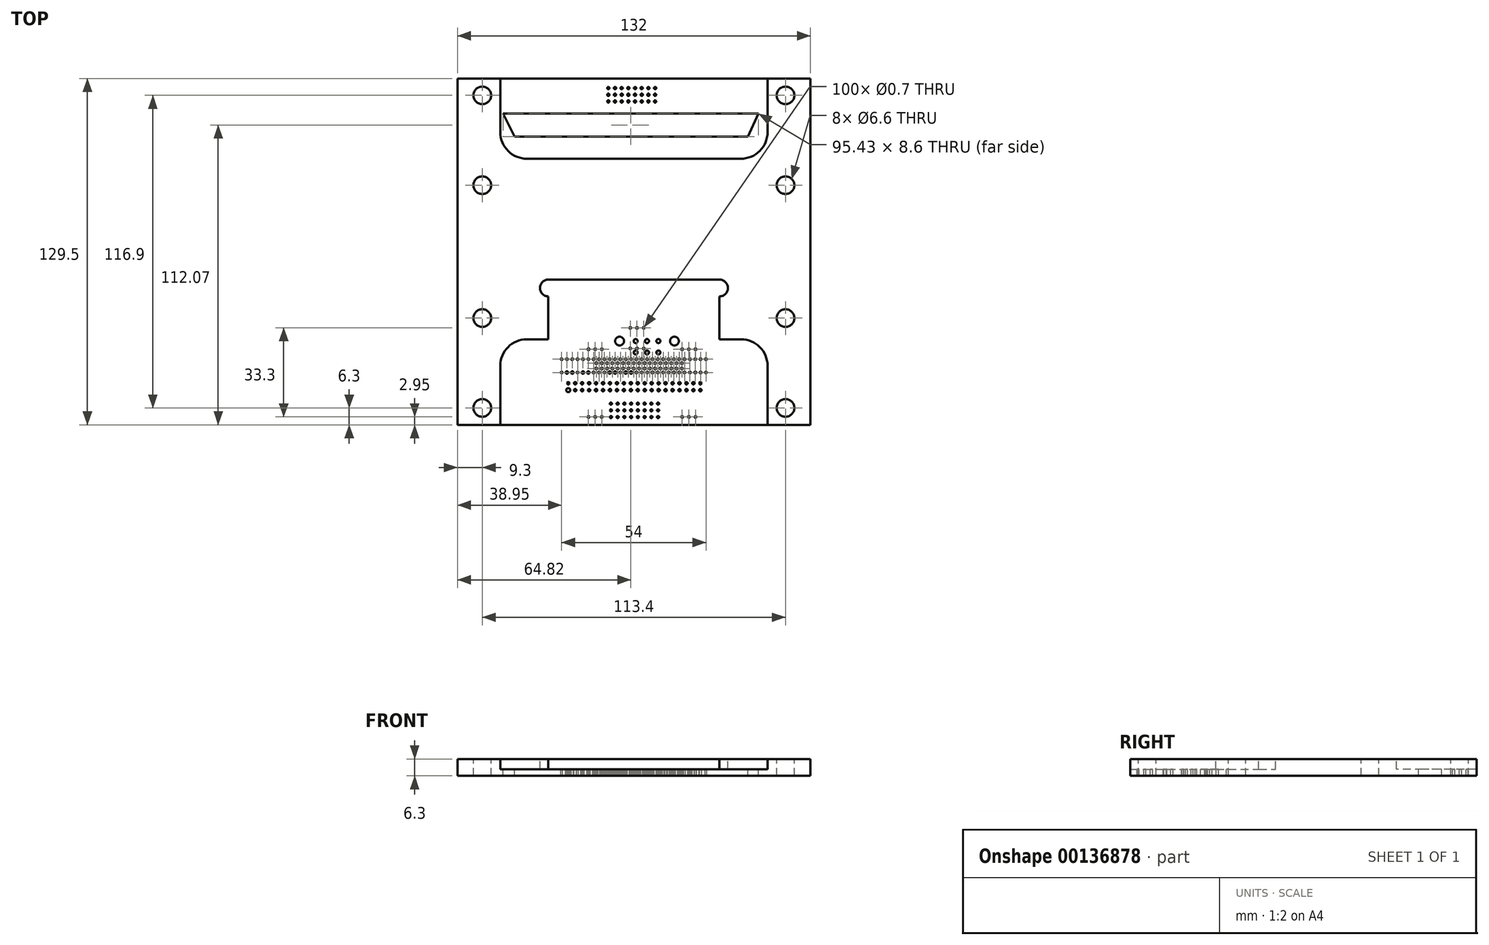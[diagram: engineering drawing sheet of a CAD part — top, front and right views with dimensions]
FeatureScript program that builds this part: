
annotation { "Feature Type Name" : "Feature", "Feature Type Description" : "" }
export const myFeature = defineFeature(function(context is Context, id is Id, definition is map)
    precondition{}
    {
        {
            var Q0;
            Q0=qCreatedBy(makeId("Top.planeOp"),FACE);
            var sketch = newSketch(context, id + "F0", { "sketchPlane" : qUnion([Q0])});
            skLineSegment(sketch, "E0.bottom", {"start": v(-66, 64.75) * mm, "end": v(66, 64.75) * mm});
            skLineSegment(sketch, "E0.top", {"start": v(-66, -64.75) * mm, "end": v(66, -64.75) * mm});
            skLineSegment(sketch, "E0.left", {"start": v(-66, 64.75) * mm, "end": v(-66, -64.75) * mm});
            skLineSegment(sketch, "E0.right", {"start": v(66, 64.75) * mm, "end": v(66, -64.75) * mm});
            skPoint(sketch, "E0.middle", {"position": v(0, 0) * mm});
            skSolve(sketch);
        }
        {
            var Q0;
            Q0 = qSketchRegion(id + "F0", true);
            extrude(context, id + "F1", {"entities" : qUnion([Q0]), "depth" : 6.3 * mm});
        }
        {
            var Q0;
            Q0=makeQuery(id+"F1.opExtrude","CAP_FACE",FACE,{"disambiguationData":[OSD([sQuery(id+"F0.wireOp",EDGE,"E0.bottom"),sQuery(id+"F0.wireOp",EDGE,"E0.top"),sQuery(id+"F0.wireOp",EDGE,"E0.left"),sQuery(id+"F0.wireOp",EDGE,"E0.right")])],"isStart":false});
            var sketch = newSketch(context, id + "F2", { "sketchPlane" : qUnion([Q0])});
            skLineSegment(sketch, "E1.bottom", {"start": v(-50, -64.75) * mm, "end": v(50, -64.75) * mm});
            skLineSegment(sketch, "E1.top", {"start": v(-40, -32.75) * mm, "end": v(-32, -32.75) * mm});
            skLineSegment(sketch, "E1.left", {"start": v(-50, -64.75) * mm, "end": v(-50, -42.75) * mm});
            skLineSegment(sketch, "E1.right", {"start": v(50, -64.75) * mm, "end": v(50, -42.75) * mm});
            skPoint(sketch, "E2.visualSharp", {"position": v(-50, -32.75) * mm});
            skArc(sketch, "E2.filletArc", {"start": v(-40, -32.75) * mm, "mid": v(-47.07, -35.68) * mm, "end": v(-50, -42.75) * mm});
            skPoint(sketch, "E3.visualSharp", {"position": v(50, -32.75) * mm});
            skArc(sketch, "E3.filletArc", {"start": v(50, -42.75) * mm, "mid": v(47.07, -35.68) * mm, "end": v(40, -32.75) * mm});
            skLineSegment(sketch, "E4.left", {"start": v(-32, -32.75) * mm, "end": v(-32, -16.75) * mm});
            skLineSegment(sketch, "E4.right", {"start": v(32, -32.75) * mm, "end": v(32, -16.75) * mm});
            skLineSegment(sketch, "E5.trimOffspring", {"start": v(32, -32.75) * mm, "end": v(40, -32.75) * mm});
            skLineSegment(sketch, "E6", {"start": v(-32, -10.45) * mm, "end": v(32, -10.45) * mm});
            skArc(sketch, "E7", {"start": v(32, -16.75) * mm, "mid": v(35.15, -13.6) * mm, "end": v(32, -10.45) * mm});
            skArc(sketch, "E8", {"start": v(-32, -10.45) * mm, "mid": v(-35.15, -13.6) * mm, "end": v(-32, -16.75) * mm});
            skLineSegment(sketch, "E9.bottom", {"start": v(-50, 64.75) * mm, "end": v(50, 64.75) * mm});
            skLineSegment(sketch, "E9.top", {"start": v(-40, 34.75) * mm, "end": v(40, 34.75) * mm});
            skLineSegment(sketch, "E9.left", {"start": v(-50, 64.75) * mm, "end": v(-50, 44.75) * mm});
            skLineSegment(sketch, "E9.right", {"start": v(50, 64.75) * mm, "end": v(50, 44.75) * mm});
            skPoint(sketch, "E10.visualSharp", {"position": v(-50, 34.75) * mm});
            skArc(sketch, "E10.filletArc", {"start": v(-50, 44.75) * mm, "mid": v(-47.07, 37.68) * mm, "end": v(-40, 34.75) * mm});
            skPoint(sketch, "E11.visualSharp", {"position": v(50, 34.75) * mm});
            skArc(sketch, "E11.filletArc", {"start": v(40, 34.75) * mm, "mid": v(47.07, 37.68) * mm, "end": v(50, 44.75) * mm});
            skSolve(sketch);
        }
        {
            var Q0;
            Q0 = qSketchRegion(id + "F2", true);
            extrude(context, id + "F3", {"entities" : qUnion([Q0]), "operationType" : NewBodyOperationType.REMOVE, "oppositeDirection" : true, "depth" : 3.85 * mm});
        }
        {
            var Q0;
            Q0=makeQuery(id+"F3.boolean.opBoolean","COPY",FACE,{"derivedFrom":makeQuery(id+"F3.opExtrude","CAP_FACE",FACE,{"disambiguationData":[OSD([sQuery(id+"F2.wireOp",EDGE,"E9.bottom"),sQuery(id+"F2.wireOp",EDGE,"E9.top"),sQuery(id+"F2.wireOp",EDGE,"E9.left"),sQuery(id+"F2.wireOp",EDGE,"E9.right"),sQuery(id+"F2.wireOp",EDGE,"E10.filletArc"),sQuery(id+"F2.wireOp",EDGE,"E11.filletArc")])],"isStart":false})});
            var sketch = newSketch(context, id + "F4", { "sketchPlane" : qUnion([Q0])});
            skLineSegment(sketch, "E12.bottom", {"start": v(-48.9, 51.62) * mm, "end": v(46.54, 51.62) * mm});
            skLineSegment(sketch, "E12.top", {"start": v(-44.65, 43.02) * mm, "end": v(42.68, 43.02) * mm});
            skLineSegment(sketch, "E13", {"start": v(46.54, 51.62) * mm, "end": v(42.68, 43.02) * mm});
            skLineSegment(sketch, "E14", {"start": v(-48.9, 51.62) * mm, "end": v(-44.65, 43.02) * mm});
            skSolve(sketch);
        }
        {
            var Q0;
            Q0 = qSketchRegion(id + "F4", true);
            extrude(context, id + "F5", {"entities" : qUnion([Q0]), "operationType" : NewBodyOperationType.REMOVE, "oppositeDirection" : true, "depth" : 25 * mm});
        }
        {
            var Q0;
            Q0=makeQuery(id+"F1.opExtrude","CAP_FACE",FACE,{"disambiguationData":[OSD([sQuery(id+"F0.wireOp",EDGE,"E0.bottom"),sQuery(id+"F0.wireOp",EDGE,"E0.top"),sQuery(id+"F0.wireOp",EDGE,"E0.left"),sQuery(id+"F0.wireOp",EDGE,"E0.right")])],"isStart":false});
            var sketch = newSketch(context, id + "F6", { "sketchPlane" : qUnion([Q0])});
            skCircle(sketch, "E15", {"center": v(-56.7, 58.45) * mm, "radius": 3.3 * mm});
            skCircle(sketch, "E16", {"center": v(-56.7, 24.85) * mm, "radius": 3.3 * mm});
            skCircle(sketch, "E17", {"center": v(-56.7, -24.85) * mm, "radius": 3.3 * mm});
            skCircle(sketch, "E18", {"center": v(-56.7, -58.45) * mm, "radius": 3.3 * mm});
            skCircle(sketch, "E19", {"center": v(56.7, -58.45) * mm, "radius": 3.3 * mm});
            skCircle(sketch, "E20", {"center": v(56.7, -24.85) * mm, "radius": 3.3 * mm});
            skCircle(sketch, "E21", {"center": v(56.7, 24.85) * mm, "radius": 3.3 * mm});
            skCircle(sketch, "E22", {"center": v(56.7, 58.45) * mm, "radius": 3.3 * mm});
            skSolve(sketch);
        }
        {
            var Q0;
            Q0 = qSketchRegion(id + "F6", true);
            extrude(context, id + "F7", {"entities" : qUnion([Q0]), "operationType" : NewBodyOperationType.REMOVE, "oppositeDirection" : true, "depth" : 25 * mm});
        }
        {
            var Q0;
            Q0=makeQuery(id+"F3.boolean.opBoolean","COPY",FACE,{"derivedFrom":makeQuery(id+"F3.opExtrude","CAP_FACE",FACE,{"disambiguationData":[OSD([sQuery(id+"F2.wireOp",EDGE,"E9.bottom"),sQuery(id+"F2.wireOp",EDGE,"E9.top"),sQuery(id+"F2.wireOp",EDGE,"E9.left"),sQuery(id+"F2.wireOp",EDGE,"E9.right"),sQuery(id+"F2.wireOp",EDGE,"E10.filletArc"),sQuery(id+"F2.wireOp",EDGE,"E11.filletArc")])],"isStart":false})});
            var sketch = newSketch(context, id + "F8", { "sketchPlane" : qUnion([Q0])});
            skCircle(sketch, "E23", {"center": v(-9.58, 61.17) * mm, "radius": 0.42 * mm});
            skCircle(sketch, "E24", {"center": v(-8.6, -61.85) * mm, "radius": 0.4 * mm});
            skCircle(sketch, "E25.0.1.0", {"center": v(-8.6, -59.35) * mm, "radius": 0.4 * mm});
            skCircle(sketch, "E25.0.2.0", {"center": v(-8.6, -56.85) * mm, "radius": 0.4 * mm});
            skCircle(sketch, "E25.1.0.0", {"center": v(-6.08, -61.85) * mm, "radius": 0.4 * mm});
            skCircle(sketch, "E25.1.1.0", {"center": v(-6.08, -59.35) * mm, "radius": 0.4 * mm});
            skCircle(sketch, "E25.1.2.0", {"center": v(-6.08, -56.85) * mm, "radius": 0.4 * mm});
            skCircle(sketch, "E25.2.0.0", {"center": v(-3.56, -61.85) * mm, "radius": 0.4 * mm});
            skCircle(sketch, "E25.2.1.0", {"center": v(-3.56, -59.35) * mm, "radius": 0.4 * mm});
            skCircle(sketch, "E25.2.2.0", {"center": v(-3.56, -56.85) * mm, "radius": 0.4 * mm});
            skCircle(sketch, "E25.3.0.0", {"center": v(-1.04, -61.85) * mm, "radius": 0.4 * mm});
            skCircle(sketch, "E25.3.1.0", {"center": v(-1.04, -59.35) * mm, "radius": 0.4 * mm});
            skCircle(sketch, "E25.3.2.0", {"center": v(-1.04, -56.85) * mm, "radius": 0.4 * mm});
            skCircle(sketch, "E25.4.0.0", {"center": v(1.48, -61.85) * mm, "radius": 0.4 * mm});
            skCircle(sketch, "E25.4.1.0", {"center": v(1.48, -59.35) * mm, "radius": 0.4 * mm});
            skCircle(sketch, "E25.4.2.0", {"center": v(1.48, -56.85) * mm, "radius": 0.4 * mm});
            skCircle(sketch, "E25.5.0.0", {"center": v(4, -61.85) * mm, "radius": 0.4 * mm});
            skCircle(sketch, "E25.5.1.0", {"center": v(4, -59.35) * mm, "radius": 0.4 * mm});
            skCircle(sketch, "E25.5.2.0", {"center": v(4, -56.85) * mm, "radius": 0.4 * mm});
            skCircle(sketch, "E25.6.0.0", {"center": v(6.52, -61.85) * mm, "radius": 0.4 * mm});
            skCircle(sketch, "E25.6.1.0", {"center": v(6.52, -59.35) * mm, "radius": 0.4 * mm});
            skCircle(sketch, "E25.6.2.0", {"center": v(6.52, -56.85) * mm, "radius": 0.4 * mm});
            skCircle(sketch, "E25.7.0.0", {"center": v(9.04, -61.85) * mm, "radius": 0.4 * mm});
            skCircle(sketch, "E25.7.1.0", {"center": v(9.04, -59.35) * mm, "radius": 0.4 * mm});
            skCircle(sketch, "E25.7.2.0", {"center": v(9.04, -56.85) * mm, "radius": 0.4 * mm});
            skLineSegment(sketch, "E25.direction1", {"start": v(-8.6, -61.85) * mm, "end": v(-6.08, -61.85) * mm, "construction": true});
            skLineSegment(sketch, "E25.direction2", {"start": v(-8.6, -61.85) * mm, "end": v(-8.6, -59.35) * mm, "construction": true});
            skCircle(sketch, "E26.0.1.0", {"center": v(-9.58, 58.67) * mm, "radius": 0.42 * mm});
            skCircle(sketch, "E26.0.2.0", {"center": v(-9.58, 56.17) * mm, "radius": 0.42 * mm});
            skCircle(sketch, "E26.1.0.0", {"center": v(-7.08, 61.17) * mm, "radius": 0.42 * mm});
            skCircle(sketch, "E26.1.1.0", {"center": v(-7.08, 58.67) * mm, "radius": 0.42 * mm});
            skCircle(sketch, "E26.1.2.0", {"center": v(-7.08, 56.17) * mm, "radius": 0.42 * mm});
            skCircle(sketch, "E26.2.0.0", {"center": v(-4.58, 61.17) * mm, "radius": 0.42 * mm});
            skCircle(sketch, "E26.2.1.0", {"center": v(-4.58, 58.67) * mm, "radius": 0.42 * mm});
            skCircle(sketch, "E26.2.2.0", {"center": v(-4.58, 56.17) * mm, "radius": 0.42 * mm});
            skCircle(sketch, "E26.3.0.0", {"center": v(-2.08, 61.17) * mm, "radius": 0.42 * mm});
            skCircle(sketch, "E26.3.1.0", {"center": v(-2.08, 58.67) * mm, "radius": 0.42 * mm});
            skCircle(sketch, "E26.3.2.0", {"center": v(-2.08, 56.17) * mm, "radius": 0.42 * mm});
            skCircle(sketch, "E26.4.0.0", {"center": v(0.43, 61.17) * mm, "radius": 0.42 * mm});
            skCircle(sketch, "E26.4.1.0", {"center": v(0.43, 58.67) * mm, "radius": 0.42 * mm});
            skCircle(sketch, "E26.4.2.0", {"center": v(0.43, 56.17) * mm, "radius": 0.42 * mm});
            skCircle(sketch, "E26.5.0.0", {"center": v(2.93, 61.17) * mm, "radius": 0.42 * mm});
            skCircle(sketch, "E26.5.1.0", {"center": v(2.93, 58.67) * mm, "radius": 0.42 * mm});
            skCircle(sketch, "E26.5.2.0", {"center": v(2.93, 56.17) * mm, "radius": 0.42 * mm});
            skCircle(sketch, "E26.6.0.0", {"center": v(5.43, 61.17) * mm, "radius": 0.42 * mm});
            skCircle(sketch, "E26.6.1.0", {"center": v(5.43, 58.67) * mm, "radius": 0.42 * mm});
            skCircle(sketch, "E26.6.2.0", {"center": v(5.43, 56.17) * mm, "radius": 0.42 * mm});
            skCircle(sketch, "E26.7.0.0", {"center": v(7.92, 61.17) * mm, "radius": 0.42 * mm});
            skCircle(sketch, "E26.7.1.0", {"center": v(7.92, 58.67) * mm, "radius": 0.42 * mm});
            skCircle(sketch, "E26.7.2.0", {"center": v(7.92, 56.17) * mm, "radius": 0.42 * mm});
            skLineSegment(sketch, "E26.direction1", {"start": v(-9.58, 61.17) * mm, "end": v(-7.08, 61.17) * mm, "construction": true});
            skLineSegment(sketch, "E26.direction2", {"start": v(-9.58, 61.17) * mm, "end": v(-9.58, 58.67) * mm, "construction": true});
            skCircle(sketch, "E27.0.1.0", {"center": v(-24.55, -49.2) * mm, "radius": 0.45 * mm});
            skCircle(sketch, "E27.1.0.0", {"center": v(-21.95, -51.8) * mm, "radius": 0.45 * mm});
            skCircle(sketch, "E27.1.1.0", {"center": v(-21.95, -49.2) * mm, "radius": 0.45 * mm});
            skCircle(sketch, "E27.2.0.0", {"center": v(-19.35, -51.8) * mm, "radius": 0.45 * mm});
            skCircle(sketch, "E27.2.1.0", {"center": v(-19.35, -49.2) * mm, "radius": 0.45 * mm});
            skCircle(sketch, "E27.3.0.0", {"center": v(-16.75, -51.8) * mm, "radius": 0.45 * mm});
            skCircle(sketch, "E27.3.1.0", {"center": v(-16.75, -49.2) * mm, "radius": 0.45 * mm});
            skCircle(sketch, "E27.4.0.0", {"center": v(-14.15, -51.8) * mm, "radius": 0.45 * mm});
            skCircle(sketch, "E27.4.1.0", {"center": v(-14.15, -49.2) * mm, "radius": 0.45 * mm});
            skCircle(sketch, "E27.5.0.0", {"center": v(-11.55, -51.8) * mm, "radius": 0.45 * mm});
            skCircle(sketch, "E27.5.1.0", {"center": v(-11.55, -49.2) * mm, "radius": 0.45 * mm});
            skCircle(sketch, "E27.6.0.0", {"center": v(-8.95, -51.8) * mm, "radius": 0.45 * mm});
            skCircle(sketch, "E27.6.1.0", {"center": v(-8.95, -49.2) * mm, "radius": 0.45 * mm});
            skCircle(sketch, "E27.7.0.0", {"center": v(-6.35, -51.8) * mm, "radius": 0.45 * mm});
            skCircle(sketch, "E27.7.1.0", {"center": v(-6.35, -49.2) * mm, "radius": 0.45 * mm});
            skCircle(sketch, "E27.8.0.0", {"center": v(-3.75, -51.8) * mm, "radius": 0.45 * mm});
            skCircle(sketch, "E27.8.1.0", {"center": v(-3.75, -49.2) * mm, "radius": 0.45 * mm});
            skCircle(sketch, "E27.9.0.0", {"center": v(-1.15, -51.8) * mm, "radius": 0.45 * mm});
            skCircle(sketch, "E27.9.1.0", {"center": v(-1.15, -49.2) * mm, "radius": 0.45 * mm});
            skCircle(sketch, "E27.10.0.0", {"center": v(1.45, -51.8) * mm, "radius": 0.45 * mm});
            skCircle(sketch, "E27.10.1.0", {"center": v(1.45, -49.2) * mm, "radius": 0.45 * mm});
            skCircle(sketch, "E27.11.0.0", {"center": v(4.05, -51.8) * mm, "radius": 0.45 * mm});
            skCircle(sketch, "E27.11.1.0", {"center": v(4.05, -49.2) * mm, "radius": 0.45 * mm});
            skCircle(sketch, "E27.12.0.0", {"center": v(6.65, -51.8) * mm, "radius": 0.45 * mm});
            skCircle(sketch, "E27.12.1.0", {"center": v(6.65, -49.2) * mm, "radius": 0.45 * mm});
            skCircle(sketch, "E27.13.0.0", {"center": v(9.25, -51.8) * mm, "radius": 0.45 * mm});
            skCircle(sketch, "E27.13.1.0", {"center": v(9.25, -49.2) * mm, "radius": 0.45 * mm});
            skCircle(sketch, "E27.14.0.0", {"center": v(11.85, -51.8) * mm, "radius": 0.45 * mm});
            skCircle(sketch, "E27.14.1.0", {"center": v(11.85, -49.2) * mm, "radius": 0.45 * mm});
            skCircle(sketch, "E27.15.0.0", {"center": v(14.45, -51.8) * mm, "radius": 0.45 * mm});
            skCircle(sketch, "E27.15.1.0", {"center": v(14.45, -49.2) * mm, "radius": 0.45 * mm});
            skCircle(sketch, "E27.16.0.0", {"center": v(17.05, -51.8) * mm, "radius": 0.45 * mm});
            skCircle(sketch, "E27.16.1.0", {"center": v(17.05, -49.2) * mm, "radius": 0.45 * mm});
            skCircle(sketch, "E27.17.0.0", {"center": v(19.65, -51.8) * mm, "radius": 0.45 * mm});
            skCircle(sketch, "E27.17.1.0", {"center": v(19.65, -49.2) * mm, "radius": 0.45 * mm});
            skCircle(sketch, "E27.18.0.0", {"center": v(22.25, -51.8) * mm, "radius": 0.45 * mm});
            skCircle(sketch, "E27.18.1.0", {"center": v(22.25, -49.2) * mm, "radius": 0.45 * mm});
            skCircle(sketch, "E27.19.0.0", {"center": v(24.85, -51.8) * mm, "radius": 0.45 * mm});
            skCircle(sketch, "E27.19.1.0", {"center": v(24.85, -49.2) * mm, "radius": 0.45 * mm});
            skLineSegment(sketch, "E27.direction1", {"start": v(-24.55, -51.8) * mm, "end": v(-21.95, -51.8) * mm, "construction": true});
            skLineSegment(sketch, "E27.direction2", {"start": v(-24.55, -51.8) * mm, "end": v(-24.55, -49.2) * mm, "construction": true});
            skCircle(sketch, "E28", {"center": v(-24.55, -51.8) * mm, "radius": 0.74 * mm});
            skCircle(sketch, "E29", {"center": v(-12, -61.8) * mm, "radius": 0.35 * mm});
            skCircle(sketch, "E30", {"center": v(-27.05, -45.2) * mm, "radius": 0.35 * mm});
            skCircle(sketch, "E31.0.1.0", {"center": v(-27.05, -40.2) * mm, "radius": 0.35 * mm});
            skCircle(sketch, "E31.1.1.0", {"center": v(-25.05, -40.2) * mm, "radius": 0.35 * mm});
            skCircle(sketch, "E31.2.1.0", {"center": v(-23.05, -40.2) * mm, "radius": 0.35 * mm});
            skCircle(sketch, "E31.3.0.0", {"center": v(-21.05, -45.2) * mm, "radius": 0.35 * mm});
            skCircle(sketch, "E31.3.1.0", {"center": v(-21.05, -40.2) * mm, "radius": 0.35 * mm});
            skCircle(sketch, "E31.4.1.0", {"center": v(-19.05, -40.2) * mm, "radius": 0.35 * mm});
            skCircle(sketch, "E31.5.1.0", {"center": v(-17.05, -40.2) * mm, "radius": 0.35 * mm});
            skCircle(sketch, "E31.6.0.0", {"center": v(-15.05, -45.2) * mm, "radius": 0.35 * mm});
            skCircle(sketch, "E31.6.1.0", {"center": v(-15.05, -40.2) * mm, "radius": 0.35 * mm});
            skCircle(sketch, "E31.7.0.0", {"center": v(-13.05, -45.2) * mm, "radius": 0.35 * mm});
            skCircle(sketch, "E31.7.1.0", {"center": v(-13.05, -40.2) * mm, "radius": 0.35 * mm});
            skCircle(sketch, "E31.8.0.0", {"center": v(-11.05, -45.2) * mm, "radius": 0.35 * mm});
            skCircle(sketch, "E31.8.1.0", {"center": v(-11.05, -40.2) * mm, "radius": 0.35 * mm});
            skCircle(sketch, "E31.9.1.0", {"center": v(-9.05, -40.2) * mm, "radius": 0.35 * mm});
            skCircle(sketch, "E31.10.1.0", {"center": v(-7.05, -40.2) * mm, "radius": 0.35 * mm});
            skCircle(sketch, "E31.11.0.0", {"center": v(-5.05, -45.2) * mm, "radius": 0.35 * mm});
            skCircle(sketch, "E31.11.1.0", {"center": v(-5.05, -40.2) * mm, "radius": 0.35 * mm});
            skCircle(sketch, "E31.12.1.0", {"center": v(-3.05, -40.2) * mm, "radius": 0.35 * mm});
            skCircle(sketch, "E31.13.1.0", {"center": v(-1.05, -40.2) * mm, "radius": 0.35 * mm});
            skCircle(sketch, "E31.14.0.0", {"center": v(0.95, -45.2) * mm, "radius": 0.35 * mm});
            skCircle(sketch, "E31.14.1.0", {"center": v(0.95, -40.2) * mm, "radius": 0.35 * mm});
            skCircle(sketch, "E31.15.0.0", {"center": v(2.95, -45.2) * mm, "radius": 0.35 * mm});
            skCircle(sketch, "E31.15.1.0", {"center": v(2.95, -40.2) * mm, "radius": 0.35 * mm});
            skCircle(sketch, "E31.16.0.0", {"center": v(4.95, -45.2) * mm, "radius": 0.35 * mm});
            skCircle(sketch, "E31.16.1.0", {"center": v(4.95, -40.2) * mm, "radius": 0.35 * mm});
            skCircle(sketch, "E31.17.0.0", {"center": v(6.95, -45.2) * mm, "radius": 0.35 * mm});
            skCircle(sketch, "E31.17.1.0", {"center": v(6.95, -40.2) * mm, "radius": 0.35 * mm});
            skCircle(sketch, "E31.18.0.0", {"center": v(8.95, -45.2) * mm, "radius": 0.35 * mm});
            skCircle(sketch, "E31.18.1.0", {"center": v(8.95, -40.2) * mm, "radius": 0.35 * mm});
            skCircle(sketch, "E31.19.0.0", {"center": v(10.95, -45.2) * mm, "radius": 0.35 * mm});
            skCircle(sketch, "E31.19.1.0", {"center": v(10.95, -40.2) * mm, "radius": 0.35 * mm});
            skCircle(sketch, "E31.20.0.0", {"center": v(12.95, -45.2) * mm, "radius": 0.35 * mm});
            skCircle(sketch, "E31.20.1.0", {"center": v(12.95, -40.2) * mm, "radius": 0.35 * mm});
            skCircle(sketch, "E31.21.0.0", {"center": v(14.95, -45.2) * mm, "radius": 0.35 * mm});
            skCircle(sketch, "E31.21.1.0", {"center": v(14.95, -40.2) * mm, "radius": 0.35 * mm});
            skCircle(sketch, "E31.22.0.0", {"center": v(16.95, -45.2) * mm, "radius": 0.35 * mm});
            skCircle(sketch, "E31.22.1.0", {"center": v(16.95, -40.2) * mm, "radius": 0.35 * mm});
            skCircle(sketch, "E31.23.0.0", {"center": v(18.95, -45.2) * mm, "radius": 0.35 * mm});
            skCircle(sketch, "E31.23.1.0", {"center": v(18.95, -40.2) * mm, "radius": 0.35 * mm});
            skCircle(sketch, "E31.24.0.0", {"center": v(20.95, -45.2) * mm, "radius": 0.35 * mm});
            skCircle(sketch, "E31.24.1.0", {"center": v(20.95, -40.2) * mm, "radius": 0.35 * mm});
            skCircle(sketch, "E31.25.0.0", {"center": v(22.95, -45.2) * mm, "radius": 0.35 * mm});
            skCircle(sketch, "E31.25.1.0", {"center": v(22.95, -40.2) * mm, "radius": 0.35 * mm});
            skCircle(sketch, "E31.26.0.0", {"center": v(24.95, -45.2) * mm, "radius": 0.35 * mm});
            skCircle(sketch, "E31.26.1.0", {"center": v(24.95, -40.2) * mm, "radius": 0.35 * mm});
            skCircle(sketch, "E31.27.0.0", {"center": v(26.95, -45.2) * mm, "radius": 0.35 * mm});
            skCircle(sketch, "E31.27.1.0", {"center": v(26.95, -40.2) * mm, "radius": 0.35 * mm});
            skLineSegment(sketch, "E31.direction1", {"start": v(-27.05, -45.2) * mm, "end": v(-25.05, -45.2) * mm, "construction": true});
            skLineSegment(sketch, "E31.direction2", {"start": v(-27.05, -45.2) * mm, "end": v(-27.05, -40.2) * mm, "construction": true});
            skCircle(sketch, "E32", {"center": v(-25.05, -45.2) * mm, "radius": 0.47 * mm});
            skCircle(sketch, "E33", {"center": v(-23.05, -45.2) * mm, "radius": 0.47 * mm});
            skCircle(sketch, "E34", {"center": v(-19.05, -45.2) * mm, "radius": 0.47 * mm});
            skCircle(sketch, "E35", {"center": v(-17.05, -45.2) * mm, "radius": 0.47 * mm});
            skCircle(sketch, "E36", {"center": v(-9.05, -45.2) * mm, "radius": 0.47 * mm});
            skCircle(sketch, "E37", {"center": v(-7.05, -45.2) * mm, "radius": 0.47 * mm});
            skCircle(sketch, "E38", {"center": v(-3.05, -45.2) * mm, "radius": 0.47 * mm});
            skCircle(sketch, "E39", {"center": v(-1.05, -45.2) * mm, "radius": 0.47 * mm});
            skCircle(sketch, "E40", {"center": v(-14.05, -43.7) * mm, "radius": 0.35 * mm});
            skCircle(sketch, "E41.0.1.0", {"center": v(-14.05, -41.7) * mm, "radius": 0.35 * mm});
            skCircle(sketch, "E41.1.0.0", {"center": v(-12.05, -43.7) * mm, "radius": 0.35 * mm});
            skCircle(sketch, "E41.1.1.0", {"center": v(-12.05, -41.7) * mm, "radius": 0.35 * mm});
            skCircle(sketch, "E41.2.0.0", {"center": v(-10.05, -43.7) * mm, "radius": 0.35 * mm});
            skCircle(sketch, "E41.2.1.0", {"center": v(-10.05, -41.7) * mm, "radius": 0.35 * mm});
            skCircle(sketch, "E41.3.0.0", {"center": v(-8.05, -43.7) * mm, "radius": 0.35 * mm});
            skCircle(sketch, "E41.3.1.0", {"center": v(-8.05, -41.7) * mm, "radius": 0.35 * mm});
            skCircle(sketch, "E41.4.0.0", {"center": v(-6.05, -43.7) * mm, "radius": 0.35 * mm});
            skCircle(sketch, "E41.4.1.0", {"center": v(-6.05, -41.7) * mm, "radius": 0.35 * mm});
            skCircle(sketch, "E41.5.0.0", {"center": v(-4.05, -43.7) * mm, "radius": 0.35 * mm});
            skCircle(sketch, "E41.5.1.0", {"center": v(-4.05, -41.7) * mm, "radius": 0.35 * mm});
            skCircle(sketch, "E41.6.0.0", {"center": v(-2.05, -43.7) * mm, "radius": 0.35 * mm});
            skCircle(sketch, "E41.6.1.0", {"center": v(-2.05, -41.7) * mm, "radius": 0.35 * mm});
            skCircle(sketch, "E41.7.0.0", {"center": v(-0.05, -43.7) * mm, "radius": 0.35 * mm});
            skCircle(sketch, "E41.7.1.0", {"center": v(-0.05, -41.7) * mm, "radius": 0.35 * mm});
            skCircle(sketch, "E41.8.0.0", {"center": v(1.95, -43.7) * mm, "radius": 0.35 * mm});
            skCircle(sketch, "E41.8.1.0", {"center": v(1.95, -41.7) * mm, "radius": 0.35 * mm});
            skCircle(sketch, "E41.9.0.0", {"center": v(3.95, -43.7) * mm, "radius": 0.35 * mm});
            skCircle(sketch, "E41.9.1.0", {"center": v(3.95, -41.7) * mm, "radius": 0.35 * mm});
            skCircle(sketch, "E41.10.0.0", {"center": v(5.95, -43.7) * mm, "radius": 0.35 * mm});
            skCircle(sketch, "E41.10.1.0", {"center": v(5.95, -41.7) * mm, "radius": 0.35 * mm});
            skCircle(sketch, "E41.11.0.0", {"center": v(7.95, -43.7) * mm, "radius": 0.35 * mm});
            skCircle(sketch, "E41.11.1.0", {"center": v(7.95, -41.7) * mm, "radius": 0.35 * mm});
            skCircle(sketch, "E41.12.0.0", {"center": v(9.95, -43.7) * mm, "radius": 0.35 * mm});
            skCircle(sketch, "E41.12.1.0", {"center": v(9.95, -41.7) * mm, "radius": 0.35 * mm});
            skCircle(sketch, "E41.13.0.0", {"center": v(11.95, -43.7) * mm, "radius": 0.35 * mm});
            skCircle(sketch, "E41.13.1.0", {"center": v(11.95, -41.7) * mm, "radius": 0.35 * mm});
            skCircle(sketch, "E41.14.0.0", {"center": v(13.95, -43.7) * mm, "radius": 0.35 * mm});
            skCircle(sketch, "E41.14.1.0", {"center": v(13.95, -41.7) * mm, "radius": 0.35 * mm});
            skCircle(sketch, "E41.15.0.0", {"center": v(15.95, -43.7) * mm, "radius": 0.35 * mm});
            skCircle(sketch, "E41.15.1.0", {"center": v(15.95, -41.7) * mm, "radius": 0.35 * mm});
            skCircle(sketch, "E41.16.0.0", {"center": v(17.95, -43.7) * mm, "radius": 0.35 * mm});
            skCircle(sketch, "E41.16.1.0", {"center": v(17.95, -41.7) * mm, "radius": 0.35 * mm});
            skLineSegment(sketch, "E41.direction1", {"start": v(-14.05, -43.7) * mm, "end": v(-12.05, -43.7) * mm, "construction": true});
            skLineSegment(sketch, "E41.direction2", {"start": v(-14.05, -43.7) * mm, "end": v(-14.05, -41.7) * mm, "construction": true});
            skCircle(sketch, "E42", {"center": v(0.65, -37.7) * mm, "radius": 0.75 * mm});
            skCircle(sketch, "E43.0.1.0", {"center": v(0.65, -33.45) * mm, "radius": 0.75 * mm});
            skCircle(sketch, "E43.1.0.0", {"center": v(4.9, -37.7) * mm, "radius": 0.75 * mm});
            skCircle(sketch, "E43.1.1.0", {"center": v(4.9, -33.45) * mm, "radius": 0.75 * mm});
            skCircle(sketch, "E43.2.0.0", {"center": v(9.15, -37.7) * mm, "radius": 0.75 * mm});
            skCircle(sketch, "E43.2.1.0", {"center": v(9.15, -33.45) * mm, "radius": 0.75 * mm});
            skLineSegment(sketch, "E43.direction1", {"start": v(0.65, -37.7) * mm, "end": v(4.9, -37.7) * mm, "construction": true});
            skLineSegment(sketch, "E43.direction2", {"start": v(0.65, -37.7) * mm, "end": v(0.65, -33.45) * mm, "construction": true});
            skCircle(sketch, "E44.0.1.0", {"center": v(-12, -36.5) * mm, "radius": 0.35 * mm});
            skCircle(sketch, "E44.1.0.0", {"center": v(-14.5, -61.8) * mm, "radius": 0.35 * mm});
            skCircle(sketch, "E44.1.1.0", {"center": v(-14.5, -36.5) * mm, "radius": 0.35 * mm});
            skCircle(sketch, "E44.2.0.0", {"center": v(-17, -61.8) * mm, "radius": 0.35 * mm});
            skCircle(sketch, "E44.2.1.0", {"center": v(-17, -36.5) * mm, "radius": 0.35 * mm});
            skLineSegment(sketch, "E44.direction1", {"start": v(-12, -61.8) * mm, "end": v(-14.5, -61.8) * mm, "construction": true});
            skLineSegment(sketch, "E44.direction2", {"start": v(-12, -61.8) * mm, "end": v(-12, -36.5) * mm, "construction": true});
            skCircle(sketch, "E45", {"center": v(18.04, -61.8) * mm, "radius": 0.35 * mm});
            skCircle(sketch, "E46.0.1.0", {"center": v(18.04, -36.5) * mm, "radius": 0.35 * mm});
            skCircle(sketch, "E46.1.0.0", {"center": v(20.54, -61.8) * mm, "radius": 0.35 * mm});
            skCircle(sketch, "E46.1.1.0", {"center": v(20.54, -36.5) * mm, "radius": 0.35 * mm});
            skCircle(sketch, "E46.2.0.0", {"center": v(23.04, -61.8) * mm, "radius": 0.35 * mm});
            skCircle(sketch, "E46.2.1.0", {"center": v(23.04, -36.5) * mm, "radius": 0.35 * mm});
            skLineSegment(sketch, "E46.direction1", {"start": v(18.04, -61.8) * mm, "end": v(20.54, -61.8) * mm, "construction": true});
            skLineSegment(sketch, "E46.direction2", {"start": v(18.04, -61.8) * mm, "end": v(18.04, -36.5) * mm, "construction": true});
            skCircle(sketch, "E47", {"center": v(-1.35, -36.2) * mm, "radius": 0.35 * mm});
            skCircle(sketch, "E48.0.1.0", {"center": v(-1.35, -28.5) * mm, "radius": 0.35 * mm});
            skCircle(sketch, "E48.1.0.0", {"center": v(1.15, -36.2) * mm, "radius": 0.35 * mm});
            skCircle(sketch, "E48.1.1.0", {"center": v(1.15, -28.5) * mm, "radius": 0.35 * mm});
            skCircle(sketch, "E48.2.0.0", {"center": v(3.65, -36.2) * mm, "radius": 0.35 * mm});
            skCircle(sketch, "E48.2.1.0", {"center": v(3.65, -28.5) * mm, "radius": 0.35 * mm});
            skLineSegment(sketch, "E48.direction1", {"start": v(-1.35, -36.2) * mm, "end": v(1.15, -36.2) * mm, "construction": true});
            skLineSegment(sketch, "E48.direction2", {"start": v(-1.35, -36.2) * mm, "end": v(-1.35, -28.5) * mm, "construction": true});
            skCircle(sketch, "E49", {"center": v(15.15, -33.45) * mm, "radius": 1.65 * mm});
            skCircle(sketch, "E50", {"center": v(-5.35, -33.45) * mm, "radius": 1.65 * mm});
            skSolve(sketch);
        }
        {
            var Q0;
            Q0 = qSketchRegion(id + "F8", true);
            extrude(context, id + "F9", {"entities" : qUnion([Q0]), "operationType" : NewBodyOperationType.REMOVE, "oppositeDirection" : true, "depth" : 25 * mm});
        }
    });
